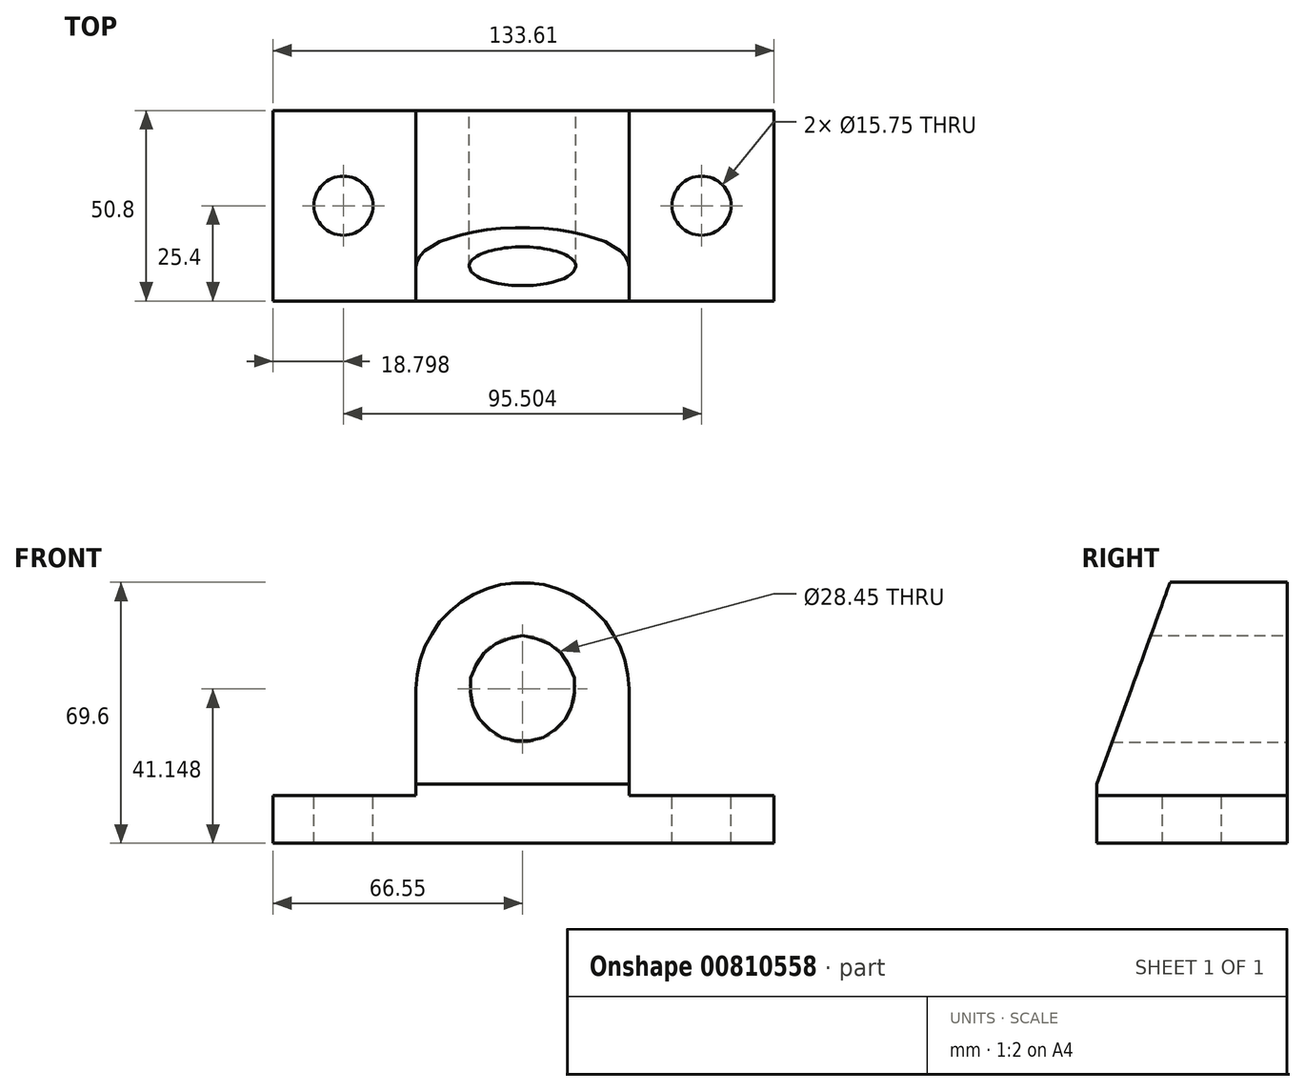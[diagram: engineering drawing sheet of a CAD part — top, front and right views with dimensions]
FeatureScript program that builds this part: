
annotation { "Feature Type Name" : "Feature", "Feature Type Description" : "" }
export const myFeature = defineFeature(function(context is Context, id is Id, definition is map)
    precondition{}
    {
        {
            var Q0;
            Q0=qCreatedBy(makeId("Front.planeOp"),FACE);
            var sketch = newSketch(context, id + "F0", { "sketchPlane" : qUnion([Q0])});
            skArc(sketch, "E0", {"start": v(28.45, 28.45) * mm, "mid": v(0, 56.9) * mm, "end": v(-28.45, 28.45) * mm});
            skCircle(sketch, "E1", {"center": v(0, 28.45) * mm, "radius": 14.22 * mm});
            skLineSegment(sketch, "E2.bottom", {"start": v(-66.55, 0) * mm, "end": v(-28.45, 0) * mm});
            skLineSegment(sketch, "E2.top", {"start": v(-66.55, -12.7) * mm, "end": v(67.06, -12.7) * mm});
            skLineSegment(sketch, "E2.left", {"start": v(-66.55, 0) * mm, "end": v(-66.55, -12.7) * mm});
            skLineSegment(sketch, "E2.right", {"start": v(67.06, 0) * mm, "end": v(67.06, -12.7) * mm});
            skLineSegment(sketch, "E3", {"start": v(-28.45, 28.45) * mm, "end": v(-28.45, 0) * mm});
            skLineSegment(sketch, "E4", {"start": v(28.45, 28.45) * mm, "end": v(28.45, 0) * mm});
            skLineSegment(sketch, "E5.trimOffspring", {"start": v(28.45, 0) * mm, "end": v(67.06, 0) * mm});
            skSolve(sketch);
        }
        {
            var Q0;
            Q0=makeQuery(id+"F0.imprint","IMPRINT",FACE,{"disambiguationData":[TD([[makeQuery(id+"F0.imprint","IMPRINT",EDGE,{"derivedFrom":sQuery(id+"F0.wireOp",EDGE,"E0")}),1.0]])]});
            extrude(context, id + "F1", {"entities" : qUnion([Q0]), "depth" : 50.8 * mm, "offsetDistance" : 25.4 * mm});
        }
        {
            var Q0;
            Q0=makeQuery(id+"F1.opExtrude","SWEPT_FACE",FACE,{"disambiguationData":[OSD([sQuery(id+"F0.wireOp",EDGE,"E2.bottom")])]});
            var sketch = newSketch(context, id + "F2", { "sketchPlane" : qUnion([Q0])});
            skCircle(sketch, "E6", {"center": v(47.75, -25.4) * mm, "radius": 7.87 * mm});
            skCircle(sketch, "E7", {"center": v(-47.75, -25.4) * mm, "radius": 7.87 * mm});
            skSolve(sketch);
        }
        {
            var Q0;
            Q0=makeQuery(id+"F2.imprint","IMPRINT",FACE,{"disambiguationData":[TD([[makeQuery(id+"F2.imprint","IMPRINT",EDGE,{"derivedFrom":sQuery(id+"F2.wireOp",EDGE,"E7")}),1.0]])]});
            var Q1;
            Q1=makeQuery(id+"F2.imprint","IMPRINT",FACE,{"disambiguationData":[TD([[makeQuery(id+"F2.imprint","IMPRINT",EDGE,{"derivedFrom":sQuery(id+"F2.wireOp",EDGE,"E6")}),1.0]])]});
            extrude(context, id + "F3", {"entities" : qUnion([Q0, Q1]), "operationType" : NewBodyOperationType.REMOVE, "oppositeDirection" : true, "depth" : 25.4 * mm, "offsetDistance" : 25.4 * mm});
        }
        {
            var Q0;
            Q0=makeQuery(id+"F1.opExtrude","SWEPT_FACE",FACE,{"disambiguationData":[OSD([sQuery(id+"F0.wireOp",EDGE,"E4")])]});
            var sketch = newSketch(context, id + "F4", { "sketchPlane" : qUnion([Q0])});
            skLineSegment(sketch, "E8", {"start": v(-50.8, 3.05) * mm, "end": v(-24.74, 74.65) * mm});
            skLineSegment(sketch, "E9", {"start": v(-50.8, 3.05) * mm, "end": v(-50.8, 79.25) * mm});
            skLineSegment(sketch, "E10", {"start": v(-50.8, 64.04) * mm, "end": v(-26.85, 68.86) * mm});
            skSolve(sketch);
        }
        {
            var Q0;
            {var subQ0=sQuery(id+"F4.wireOp",EDGE,"yJzUVh4J-EtbF-BxPe-oYD8-q8TM9U9IrxCw");Q0=makeQuery(id+"F4.imprint","IMPRINT",FACE,{"disambiguationData":[TD([[makeQuery(id+"F4.imprint","IMPRINT",EDGE,{"derivedFrom":subQ0}),-1.0]])]});}
            var Q1;
            {var subQ0=sQuery(id+"F4.wireOp",EDGE,"E9");var subQ1=sQuery(id+"F4.wireOp",EDGE,"E8");var subQ2=sQuery(id+"F0.wireOp",EDGE,"E4");var subQ3=makeQuery(id+"F4.imprint","INTERSECT",VERTEX,{"derivedFrom":[makeQuery(id+"F1.opExtrude","CAP_EDGE",EDGE,{"disambiguationData":[OSD([subQ2])],"isStart":false}),subQ1,subQ0]});Q1=makeQuery(id+"F4.imprint","IMPRINT",FACE,{"disambiguationData":[TD([[makeQuery(id+"F4.imprint","IMPRINT",EDGE,{"disambiguationData":[TD([[subQ3,-1.0]])],"derivedFrom":subQ1}),1.0]])]});}
            var Q2;
            {var subQ0=sQuery(id+"F4.wireOp",EDGE,"E10");Q2=makeQuery(id+"F4.imprint","IMPRINT",FACE,{"disambiguationData":[TD([[makeQuery(id+"F4.imprint","IMPRINT",EDGE,{"derivedFrom":subQ0}),-1.0]])]});}
            extrude(context, id + "F5", {"entities" : qUnion([Q0, Q1, Q2]), "operationType" : NewBodyOperationType.REMOVE, "oppositeDirection" : true, "depth" : 76.2 * mm, "offsetDistance" : 25.4 * mm});
        }
    });
